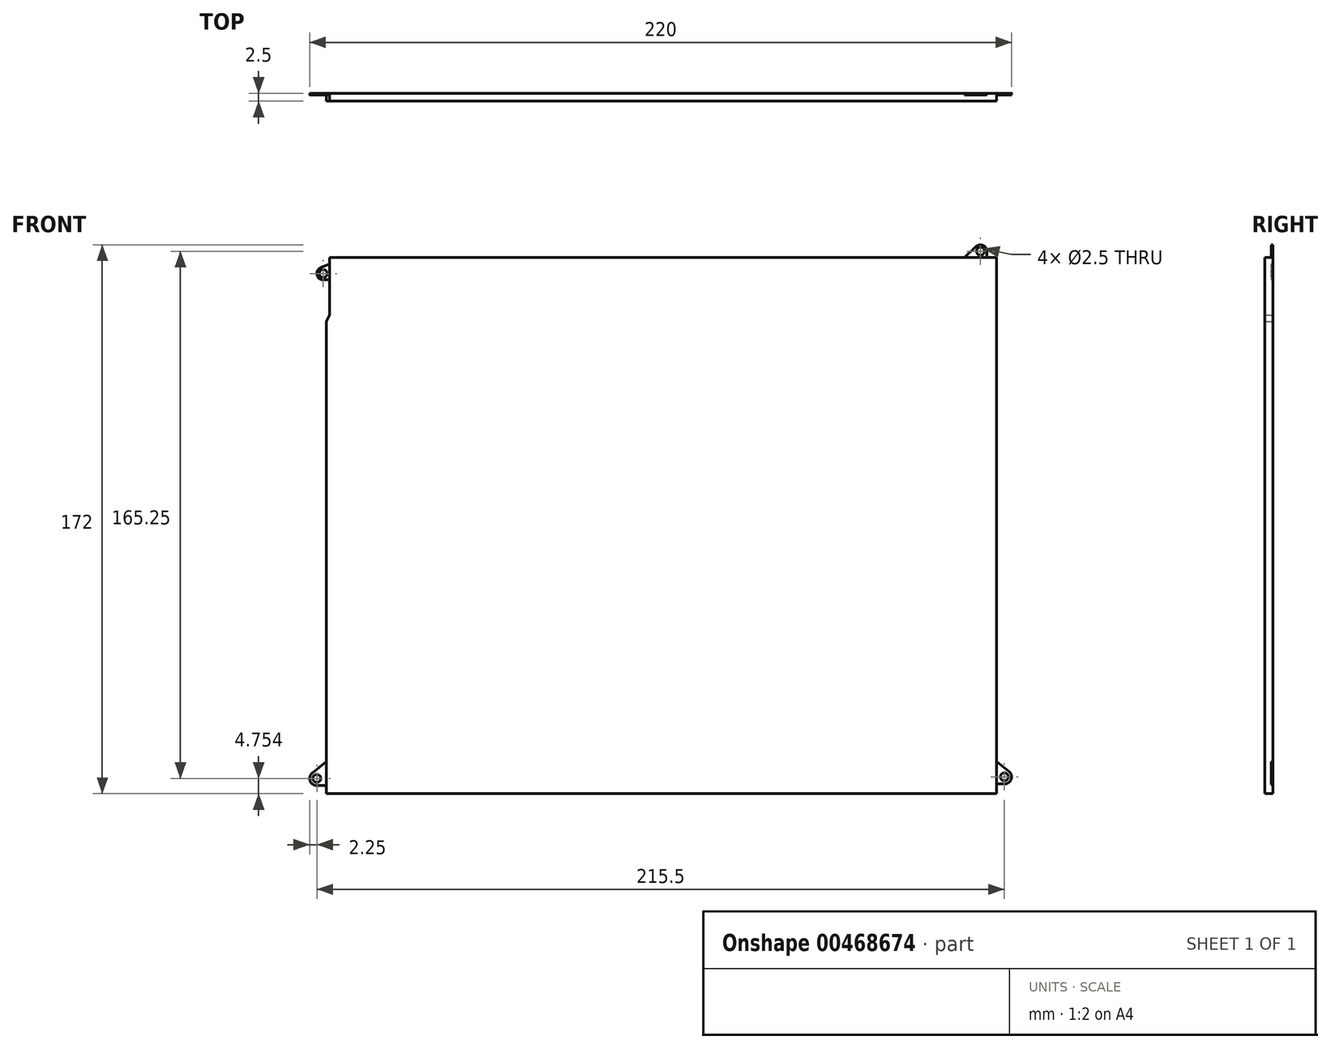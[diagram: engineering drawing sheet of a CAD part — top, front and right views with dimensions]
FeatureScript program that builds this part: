
annotation { "Feature Type Name" : "Feature", "Feature Type Description" : "" }
export const myFeature = defineFeature(function(context is Context, id is Id, definition is map)
    precondition{}
    {
        {
            var Q0;
            Q0=qCreatedBy(makeId("Front.planeOp"),FACE);
            var sketch = newSketch(context, id + "F0", { "sketchPlane" : qUnion([Q0])});
            skLineSegment(sketch, "E0.bottom", {"start": v(105, -83.84) * mm, "end": v(-105, -83.84) * mm});
            skLineSegment(sketch, "E0.top", {"start": v(105, 84.16) * mm, "end": v(-104, 84.16) * mm});
            skLineSegment(sketch, "E0.left", {"start": v(105, -83.84) * mm, "end": v(105, 84.16) * mm});
            skLineSegment(sketch, "E0.right", {"start": v(-105, -83.84) * mm, "end": v(-105, 64.16) * mm});
            skLineSegment(sketch, "E1", {"start": v(-105, -81.34) * mm, "end": v(-108.04, -81.34) * mm});
            skLineSegment(sketch, "E2", {"start": v(-105, -73.84) * mm, "end": v(-109.4, -77.32) * mm});
            skArc(sketch, "E3", {"start": v(-109.4, -77.32) * mm, "mid": v(-110.13, -79.8) * mm, "end": v(-108.04, -81.34) * mm});
            skCircle(sketch, "E4", {"center": v(-108, -79.09) * mm, "radius": 1.25 * mm});
            skCircle(sketch, "E5", {"center": v(-106, 79.16) * mm, "radius": 1.25 * mm});
            skLineSegment(sketch, "E6", {"start": v(-104, 84.16) * mm, "end": v(-104, 66.16) * mm});
            skLineSegment(sketch, "E7", {"start": v(-104, 66.16) * mm, "end": v(-105, 64.16) * mm});
            skPoint(sketch, "E8.orphan", {"position": v(-105, 84.16) * mm});
            skCircle(sketch, "E9", {"center": v(100, 86.16) * mm, "radius": 1.25 * mm});
            skLineSegment(sketch, "E10", {"start": v(98.62, 87.61) * mm, "end": v(95, 84.16) * mm});
            skLineSegment(sketch, "E11", {"start": v(102, 86.16) * mm, "end": v(102, 84.16) * mm});
            skArc(sketch, "E12", {"start": v(102, 86.16) * mm, "mid": v(100.79, 88) * mm, "end": v(98.62, 87.61) * mm});
            skCircle(sketch, "E13", {"center": v(107.5, -78.6) * mm, "radius": 1.25 * mm});
            skLineSegment(sketch, "E14", {"start": v(107.33, -80.84) * mm, "end": v(105, -80.84) * mm});
            skLineSegment(sketch, "E15", {"start": v(108.87, -76.8) * mm, "end": v(105, -73.84) * mm});
            skArc(sketch, "E16", {"start": v(107.33, -80.84) * mm, "mid": v(109.6, -79.4) * mm, "end": v(108.87, -76.8) * mm});
            skLineSegment(sketch, "E17", {"start": v(-106.77, 81.01) * mm, "end": v(-104, 82.16) * mm});
            skLineSegment(sketch, "E18", {"start": v(-106, 77.16) * mm, "end": v(-104, 77.16) * mm});
            skArc(sketch, "E19", {"start": v(-106.77, 81.01) * mm, "mid": v(-107.96, 78.77) * mm, "end": v(-106, 77.16) * mm});
            skSolve(sketch);
        }
        {
            var Q0;
            {var subQ1=sQuery(id+"F0.wireOp",EDGE,"E0.bottom");Q0=makeQuery(id+"F0.imprint","IMPRINT",FACE,{"disambiguationData":[TD([[makeQuery(id+"F0.imprint","IMPRINT",EDGE,{"derivedFrom":subQ1}),-1.0]])]});}
            extrude(context, id + "F1", {"entities" : qUnion([Q0]), "depth" : 2.5 * mm});
        }
        {
            var Q0;
            Q0=makeQuery(id+"F0.imprint","IMPRINT",FACE,{"disambiguationData":[TD([[makeQuery(id+"F0.imprint","IMPRINT",EDGE,{"derivedFrom":sQuery(id+"F0.wireOp",EDGE,"E9")}),-1.0]])]});
            var Q1;
            Q1=makeQuery(id+"F0.imprint","IMPRINT",FACE,{"disambiguationData":[TD([[makeQuery(id+"F0.imprint","IMPRINT",EDGE,{"derivedFrom":sQuery(id+"F0.wireOp",EDGE,"E5")}),-1.0]])]});
            var Q2;
            {var subQ1=sQuery(id+"F0.wireOp",EDGE,"E1");Q2=makeQuery(id+"F0.imprint","IMPRINT",FACE,{"disambiguationData":[TD([[makeQuery(id+"F0.imprint","IMPRINT",EDGE,{"derivedFrom":subQ1}),-1.0]])]});}
            var Q3;
            Q3=makeQuery(id+"F0.imprint","IMPRINT",FACE,{"disambiguationData":[TD([[makeQuery(id+"F0.imprint","IMPRINT",EDGE,{"derivedFrom":sQuery(id+"F0.wireOp",EDGE,"E13")}),-1.0]])]});
            extrude(context, id + "F2", {"entities" : qUnion([Q0, Q1, Q2, Q3]), "operationType" : NewBodyOperationType.ADD, "depth" : 0.5 * mm});
        }
        {
            var Q0;
            Q0=qCreatedBy(makeId("Front.planeOp"),FACE);
            var sketch = newSketch(context, id + "F3", { "sketchPlane" : qUnion([Q0])});
            skLineSegment(sketch, "E20.bottom", {"start": v(99, -74.84) * mm, "end": v(-101, -74.84) * mm});
            skLineSegment(sketch, "E20.top", {"start": v(99, 76.16) * mm, "end": v(-101, 76.16) * mm});
            skLineSegment(sketch, "E20.left", {"start": v(99, -74.84) * mm, "end": v(99, 76.16) * mm});
            skLineSegment(sketch, "E20.right", {"start": v(-101, -74.84) * mm, "end": v(-101, 76.16) * mm});
            skPoint(sketch, "E20.middle", {"position": v(0, 1.66) * mm});
            skSolve(sketch);
        }
        {
            var Q0;
            Q0 = qSketchRegion(id + "F3", true);
            extrude(context, id + "F4", {"entities" : qUnion([Q0]), "operationType" : NewBodyOperationType.ADD, "depth" : 0.1 * mm});
        }
    });
